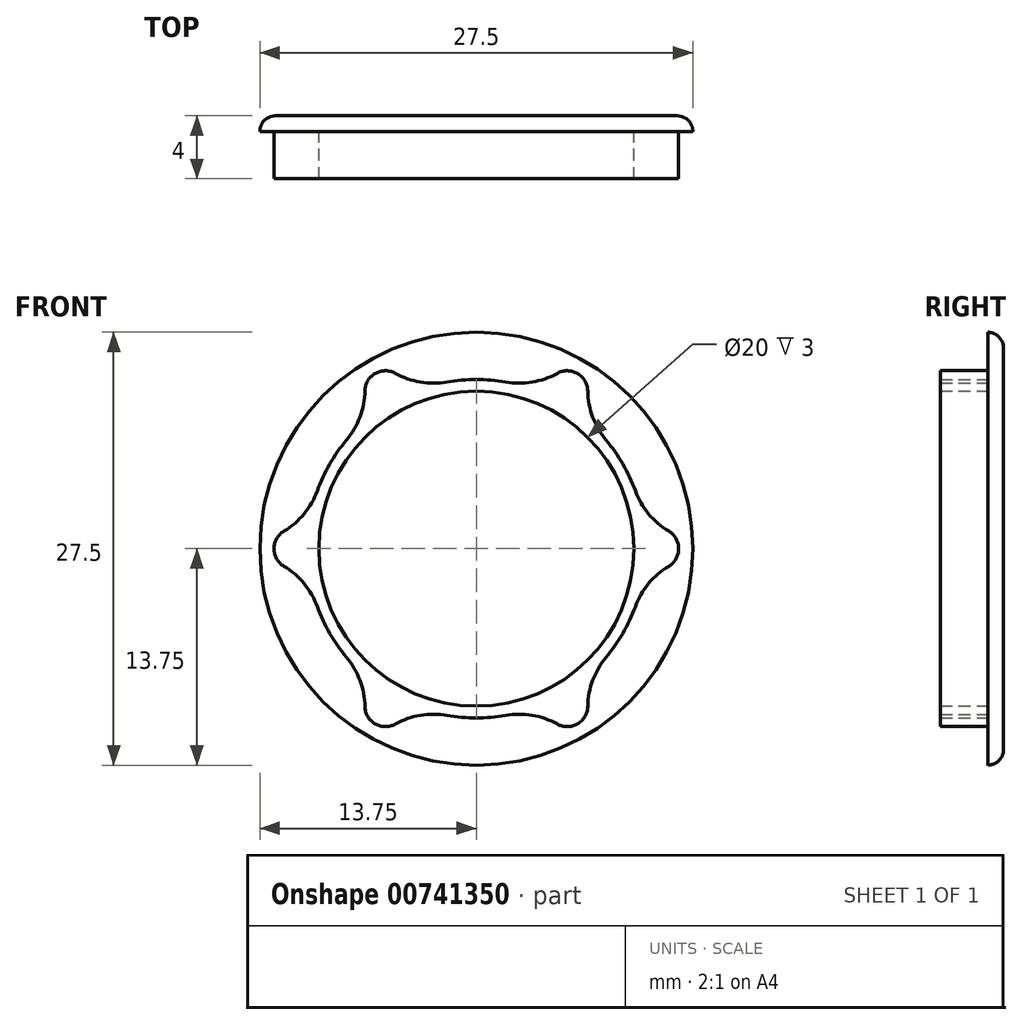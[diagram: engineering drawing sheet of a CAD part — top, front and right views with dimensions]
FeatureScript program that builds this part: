
annotation { "Feature Type Name" : "Feature", "Feature Type Description" : "" }
export const myFeature = defineFeature(function(context is Context, id is Id, definition is map)
    precondition{}
    {
        {
            var Q0;
            Q0=qCreatedBy(makeId("Front.planeOp"),FACE);
            var sketch = newSketch(context, id + "F0", { "sketchPlane" : qUnion([Q0])});
            skCircle(sketch, "E0", {"center": v(0, 0) * mm, "radius": 10 * mm});
            skCircle(sketch, "E1", {"center": v(0, 0) * mm, "radius": 13.75 * mm});
            skArc(sketch, "E2", {"start": v(-8.24, 6.9) * mm, "mid": v(-9.3, 5.37) * mm, "end": v(-10.1, 3.69) * mm});
            skPoint(sketch, "E3.0.midPoint", {"position": v(0, 10) * mm});
            skArc(sketch, "E4", {"start": v(-5.14, 11.14) * mm, "mid": v(-6.42, 11.13) * mm, "end": v(-7.08, 10.02) * mm});
            skArc(sketch, "E5", {"start": v(7.08, 10.02) * mm, "mid": v(6.42, 11.13) * mm, "end": v(5.14, 11.14) * mm});
            skArc(sketch, "E6", {"start": v(12.22, -1.12) * mm, "mid": v(12.85, 0) * mm, "end": v(12.22, 1.12) * mm});
            skArc(sketch, "E7", {"start": v(5.14, -11.14) * mm, "mid": v(6.43, -11.13) * mm, "end": v(7.08, -10.02) * mm});
            skArc(sketch, "E8", {"start": v(-7.08, -10.02) * mm, "mid": v(-6.42, -11.13) * mm, "end": v(-5.14, -11.14) * mm});
            skArc(sketch, "E9", {"start": v(-12.22, 1.12) * mm, "mid": v(-12.85, 0) * mm, "end": v(-12.22, -1.12) * mm});
            skArc(sketch, "E10.trimOffspring", {"start": v(1.86, 10.59) * mm, "mid": v(0, 10.75) * mm, "end": v(-1.86, 10.59) * mm});
            skArc(sketch, "E11.trimOffspring", {"start": v(10.1, 3.69) * mm, "mid": v(9.3, 5.38) * mm, "end": v(8.24, 6.9) * mm});
            skArc(sketch, "E12.trimOffspring", {"start": v(8.24, -6.9) * mm, "mid": v(9.3, -5.37) * mm, "end": v(10.1, -3.69) * mm});
            skArc(sketch, "E13.trimOffspring", {"start": v(-1.86, -10.59) * mm, "mid": v(0, -10.75) * mm, "end": v(1.86, -10.59) * mm});
            skArc(sketch, "E14.trimOffspring", {"start": v(-10.1, -3.69) * mm, "mid": v(-9.3, -5.38) * mm, "end": v(-8.24, -6.9) * mm});
            skPoint(sketch, "E15.visualSharp", {"position": v(-4.5, 9.77) * mm});
            skArc(sketch, "E15.filletArc", {"start": v(-5.14, 11.14) * mm, "mid": v(-3.55, 10.58) * mm, "end": v(-1.86, 10.59) * mm});
            skPoint(sketch, "E16.visualSharp", {"position": v(-6.21, 8.77) * mm});
            skArc(sketch, "E16.filletArc", {"start": v(-8.24, 6.9) * mm, "mid": v(-7.4, 8.36) * mm, "end": v(-7.08, 10.02) * mm});
            skPoint(sketch, "E17.visualSharp", {"position": v(-10.7, 1) * mm});
            skArc(sketch, "E17.filletArc", {"start": v(-12.22, 1.12) * mm, "mid": v(-10.94, 2.22) * mm, "end": v(-10.1, 3.69) * mm});
            skPoint(sketch, "E18.visualSharp", {"position": v(-10.7, -1) * mm});
            skArc(sketch, "E18.filletArc", {"start": v(-10.1, -3.69) * mm, "mid": v(-10.94, -2.22) * mm, "end": v(-12.22, -1.12) * mm});
            skPoint(sketch, "E19.visualSharp", {"position": v(-6.21, -8.77) * mm});
            skArc(sketch, "E19.filletArc", {"start": v(-7.08, -10.02) * mm, "mid": v(-7.4, -8.36) * mm, "end": v(-8.24, -6.9) * mm});
            skPoint(sketch, "E20.visualSharp", {"position": v(-4.5, -9.77) * mm});
            skArc(sketch, "E20.filletArc", {"start": v(-1.86, -10.59) * mm, "mid": v(-3.55, -10.58) * mm, "end": v(-5.14, -11.14) * mm});
            skPoint(sketch, "E21.visualSharp", {"position": v(4.5, -9.77) * mm});
            skArc(sketch, "E21.filletArc", {"start": v(5.14, -11.14) * mm, "mid": v(3.55, -10.58) * mm, "end": v(1.86, -10.59) * mm});
            skPoint(sketch, "E22.visualSharp", {"position": v(6.21, -8.77) * mm});
            skArc(sketch, "E22.filletArc", {"start": v(8.24, -6.9) * mm, "mid": v(7.4, -8.36) * mm, "end": v(7.08, -10.02) * mm});
            skPoint(sketch, "E23.visualSharp", {"position": v(10.7, -1) * mm});
            skArc(sketch, "E23.filletArc", {"start": v(12.22, -1.12) * mm, "mid": v(10.94, -2.22) * mm, "end": v(10.1, -3.69) * mm});
            skPoint(sketch, "E24.visualSharp", {"position": v(10.7, 1) * mm});
            skArc(sketch, "E24.filletArc", {"start": v(10.1, 3.69) * mm, "mid": v(10.94, 2.22) * mm, "end": v(12.22, 1.12) * mm});
            skPoint(sketch, "E25.visualSharp", {"position": v(6.21, 8.77) * mm});
            skArc(sketch, "E25.filletArc", {"start": v(7.08, 10.02) * mm, "mid": v(7.4, 8.36) * mm, "end": v(8.24, 6.9) * mm});
            skPoint(sketch, "E26.visualSharp", {"position": v(4.5, 9.77) * mm});
            skArc(sketch, "E26.filletArc", {"start": v(1.86, 10.59) * mm, "mid": v(3.55, 10.58) * mm, "end": v(5.14, 11.14) * mm});
            skSolve(sketch);
        }
        {
            var Q0;
            Q0=makeQuery(id+"F0.imprint","IMPRINT",FACE,{"disambiguationData":[TD([[makeQuery(id+"F0.imprint","IMPRINT",EDGE,{"derivedFrom":sQuery(id+"F0.wireOp",EDGE,"E0")}),-1.0]])]});
            extrude(context, id + "F1", {"entities" : qUnion([Q0]), "depth" : 3 * mm, "offsetDistance" : 25 * mm});
        }
        {
            var Q0;
            Q0=qCreatedBy(makeId("Front.planeOp"),FACE);
            var sketch = newSketch(context, id + "F2", { "sketchPlane" : qUnion([Q0])});
            skCircle(sketch, "E27", {"center": v(0, 0) * mm, "radius": 13.75 * mm});
            skSolve(sketch);
        }
        {
            var Q0;
            Q0 = qSketchRegion(id + "F2", true);
            extrude(context, id + "F3", {"entities" : qUnion([Q0]), "operationType" : NewBodyOperationType.ADD, "oppositeDirection" : true, "depth" : 1 * mm, "offsetDistance" : 25 * mm});
        }
        {
            var Q0;
            Q0=makeQuery(id+"F3.opExtrude","CAP_EDGE",EDGE,{"disambiguationData":[OSD([sQuery(id+"F2.wireOp",EDGE,"E27")])],"isStart":false});
            fillet(context, id + "F4", {"entities" : qUnion([Q0]), "radius" : 1 * mm, "tangentPropagation" : true, "allowEdgeOverflow" : false});
        }
    });
